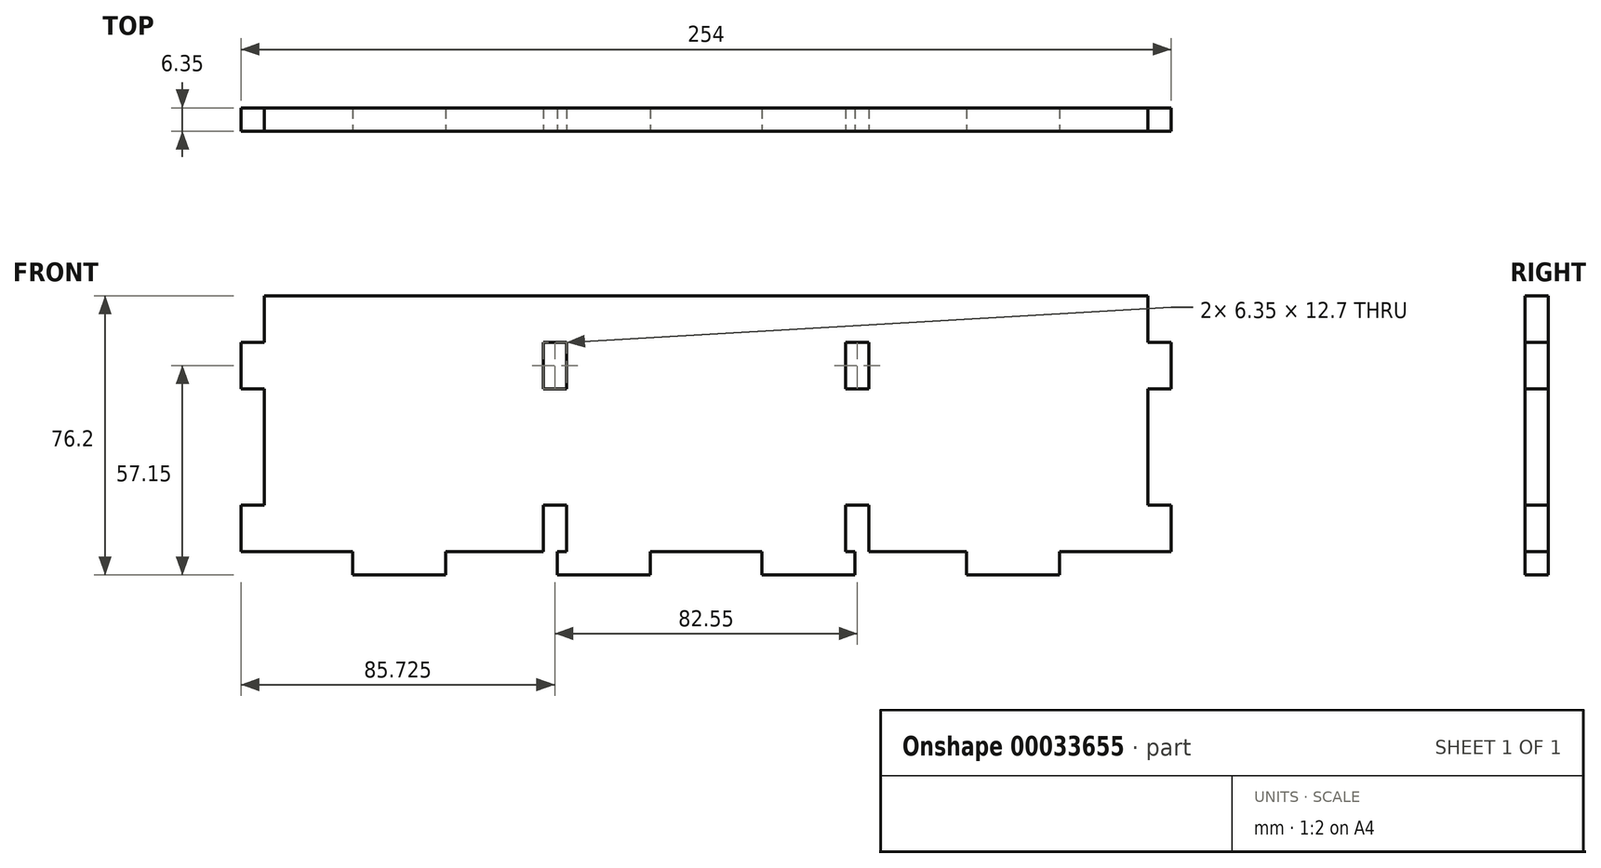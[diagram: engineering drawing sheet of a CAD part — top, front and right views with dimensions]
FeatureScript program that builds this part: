
annotation { "Feature Type Name" : "Feature", "Feature Type Description" : "" }
export const myFeature = defineFeature(function(context is Context, id is Id, definition is map)
    precondition{}
    {
        {
            var Q0;
            Q0=qCreatedBy(makeId("Front.planeOp"),FACE);
            var sketch = newSketch(context, id + "F0", { "sketchPlane" : qUnion([Q0])});
            skLineSegment(sketch, "E0.bottom", {"start": v(0, 0) * mm, "end": v(254, 0) * mm});
            skLineSegment(sketch, "E0.top", {"start": v(0, 76.2) * mm, "end": v(254, 76.2) * mm});
            skLineSegment(sketch, "E0.left", {"start": v(0, 0) * mm, "end": v(0, 76.2) * mm});
            skLineSegment(sketch, "E0.right", {"start": v(254, 0) * mm, "end": v(254, 76.2) * mm});
            skSolve(sketch);
        }
        {
            var Q0;
            Q0=makeQuery(id+"F0.imprint","IMPRINT",FACE,{"disambiguationData":[TD([[makeQuery(id+"F0.imprint","IMPRINT",EDGE,{"derivedFrom":sQuery(id+"F0.wireOp",EDGE,"E0.bottom")}),1.0]])]});
            extrude(context, id + "F1", {"entities" : qUnion([Q0]), "depth" : 6.35 * mm});
        }
        {
            var Q0;
            Q0=makeQuery(id+"F1.opExtrude","CAP_FACE",FACE,{"disambiguationData":[OSD([sQuery(id+"F0.wireOp",EDGE,"E0.bottom"),sQuery(id+"F0.wireOp",EDGE,"E0.top"),sQuery(id+"F0.wireOp",EDGE,"E0.left"),sQuery(id+"F0.wireOp",EDGE,"E0.right")])],"isStart":false});
            var sketch = newSketch(context, id + "F2", { "sketchPlane" : qUnion([Q0])});
            skLineSegment(sketch, "E1", {"start": v(127, 76.2) * mm, "end": v(127, 0) * mm, "construction": true});
            skLineSegment(sketch, "E2.bottom", {"start": v(0, 0) * mm, "end": v(6.35, 0) * mm});
            skLineSegment(sketch, "E2.top", {"start": v(0, 6.35) * mm, "end": v(6.35, 6.35) * mm});
            skLineSegment(sketch, "E2.left", {"start": v(0, 0) * mm, "end": v(0, 6.35) * mm});
            skLineSegment(sketch, "E2.right", {"start": v(6.35, 0) * mm, "end": v(6.35, 6.35) * mm});
            skLineSegment(sketch, "E3.bottom", {"start": v(0, 76.2) * mm, "end": v(6.35, 76.2) * mm});
            skLineSegment(sketch, "E3.top", {"start": v(0, 63.5) * mm, "end": v(6.35, 63.5) * mm});
            skLineSegment(sketch, "E3.left", {"start": v(0, 76.2) * mm, "end": v(0, 63.5) * mm});
            skLineSegment(sketch, "E3.right", {"start": v(6.35, 76.2) * mm, "end": v(6.35, 63.5) * mm});
            skLineSegment(sketch, "E4.bottom", {"start": v(0, 19.05) * mm, "end": v(6.35, 19.05) * mm});
            skLineSegment(sketch, "E4.top", {"start": v(0, 50.8) * mm, "end": v(6.35, 50.8) * mm});
            skLineSegment(sketch, "E4.left", {"start": v(0, 19.05) * mm, "end": v(0, 50.8) * mm});
            skLineSegment(sketch, "E4.right", {"start": v(6.35, 19.05) * mm, "end": v(6.35, 50.8) * mm});
            skLineSegment(sketch, "E5.MirrorCS", {"start": v(254, 6.35) * mm, "end": v(247.65, 6.35) * mm});
            skLineSegment(sketch, "E6.MirrorCS", {"start": v(254, 19.05) * mm, "end": v(247.65, 19.05) * mm});
            skLineSegment(sketch, "E7.MirrorCS", {"start": v(254, 50.8) * mm, "end": v(247.65, 50.8) * mm});
            skLineSegment(sketch, "E8.MirrorCS", {"start": v(254, 0) * mm, "end": v(247.65, 0) * mm});
            skLineSegment(sketch, "E9.MirrorCS", {"start": v(247.65, 76.2) * mm, "end": v(247.65, 63.5) * mm});
            skLineSegment(sketch, "E10.MirrorCS", {"start": v(247.65, 0) * mm, "end": v(247.65, 6.35) * mm});
            skLineSegment(sketch, "E11.MirrorCS", {"start": v(254, 0) * mm, "end": v(254, 6.35) * mm});
            skLineSegment(sketch, "E12.MirrorCS", {"start": v(254, 63.5) * mm, "end": v(247.65, 63.5) * mm});
            skLineSegment(sketch, "E13.MirrorCS", {"start": v(254, 76.2) * mm, "end": v(247.65, 76.2) * mm});
            skLineSegment(sketch, "E14.MirrorCS", {"start": v(254, 76.2) * mm, "end": v(254, 63.5) * mm});
            skLineSegment(sketch, "E15.MirrorCS", {"start": v(247.65, 19.05) * mm, "end": v(247.65, 50.8) * mm});
            skLineSegment(sketch, "E16.MirrorCS", {"start": v(254, 19.05) * mm, "end": v(254, 50.8) * mm});
            skSolve(sketch);
        }
        {
            var Q0;
            Q0=qSketchRegion(id+"F2",true);
            extrude(context, id + "F3", {"entities" : qUnion([Q0]), "operationType" : NewBodyOperationType.REMOVE, "endBound" : BoundingType.UP_TO_NEXT, "oppositeDirection" : true, "depth" : 25.4 * mm});
        }
        {
            var Q0;
            Q0=makeQuery(id+"F1.opExtrude","CAP_FACE",FACE,{"disambiguationData":[OSD([sQuery(id+"F0.wireOp",EDGE,"E0.bottom"),sQuery(id+"F0.wireOp",EDGE,"E0.top"),sQuery(id+"F0.wireOp",EDGE,"E0.left"),sQuery(id+"F0.wireOp",EDGE,"E0.right")])],"isStart":false});
            var sketch = newSketch(context, id + "F4", { "sketchPlane" : qUnion([Q0])});
            skLineSegment(sketch, "E17.bottom", {"start": v(0, 0) * mm, "end": v(30.48, 0) * mm});
            skLineSegment(sketch, "E17.top", {"start": v(0, 6.35) * mm, "end": v(30.48, 6.35) * mm});
            skLineSegment(sketch, "E17.left", {"start": v(0, 0) * mm, "end": v(0, 6.35) * mm});
            skLineSegment(sketch, "E17.right", {"start": v(30.48, 0) * mm, "end": v(30.48, 6.35) * mm});
            skLineSegment(sketch, "E18.1.0.0", {"start": v(86.36, 0) * mm, "end": v(86.36, 6.35) * mm});
            skLineSegment(sketch, "E18.1.0.1", {"start": v(55.88, 0) * mm, "end": v(55.88, 6.35) * mm});
            skLineSegment(sketch, "E18.1.0.2", {"start": v(55.88, 6.35) * mm, "end": v(86.36, 6.35) * mm});
            skLineSegment(sketch, "E18.1.0.3", {"start": v(55.88, 0) * mm, "end": v(86.36, 0) * mm});
            skLineSegment(sketch, "E18.2.0.0", {"start": v(142.24, 0) * mm, "end": v(142.24, 6.35) * mm});
            skLineSegment(sketch, "E18.2.0.1", {"start": v(111.76, 0) * mm, "end": v(111.76, 6.35) * mm});
            skLineSegment(sketch, "E18.2.0.2", {"start": v(111.76, 6.35) * mm, "end": v(142.24, 6.35) * mm});
            skLineSegment(sketch, "E18.2.0.3", {"start": v(111.76, 0) * mm, "end": v(142.24, 0) * mm});
            skLineSegment(sketch, "E18.3.0.0", {"start": v(198.12, 0) * mm, "end": v(198.12, 6.35) * mm});
            skLineSegment(sketch, "E18.3.0.1", {"start": v(167.64, 0) * mm, "end": v(167.64, 6.35) * mm});
            skLineSegment(sketch, "E18.3.0.2", {"start": v(167.64, 6.35) * mm, "end": v(198.12, 6.35) * mm});
            skLineSegment(sketch, "E18.3.0.3", {"start": v(167.64, 0) * mm, "end": v(198.12, 0) * mm});
            skLineSegment(sketch, "E18.4.0.0", {"start": v(254, 0) * mm, "end": v(254, 6.35) * mm});
            skLineSegment(sketch, "E18.4.0.1", {"start": v(223.52, 0) * mm, "end": v(223.52, 6.35) * mm});
            skLineSegment(sketch, "E18.4.0.2", {"start": v(223.52, 6.35) * mm, "end": v(254, 6.35) * mm});
            skLineSegment(sketch, "E18.4.0.3", {"start": v(223.52, 0) * mm, "end": v(254, 0) * mm});
            skLineSegment(sketch, "E18.direction1", {"start": v(30.48, 0) * mm, "end": v(86.36, 0) * mm, "construction": true});
            skSolve(sketch);
        }
        {
            var Q0;
            Q0=qSketchRegion(id+"F4",true);
            extrude(context, id + "F5", {"entities" : qUnion([Q0]), "operationType" : NewBodyOperationType.REMOVE, "endBound" : BoundingType.THROUGH_ALL, "oppositeDirection" : true, "depth" : 25.4 * mm});
        }
        {
            var Q0;
            Q0=makeQuery(id+"F1.opExtrude","CAP_FACE",FACE,{"disambiguationData":[OSD([sQuery(id+"F0.wireOp",EDGE,"E0.bottom"),sQuery(id+"F0.wireOp",EDGE,"E0.top"),sQuery(id+"F0.wireOp",EDGE,"E0.left"),sQuery(id+"F0.wireOp",EDGE,"E0.right")])],"isStart":false});
            var sketch = newSketch(context, id + "F6", { "sketchPlane" : qUnion([Q0])});
            skLineSegment(sketch, "E19.bottom", {"start": v(82.55, 6.35) * mm, "end": v(88.9, 6.35) * mm});
            skLineSegment(sketch, "E19.top", {"start": v(82.55, 19.05) * mm, "end": v(88.9, 19.05) * mm});
            skLineSegment(sketch, "E19.left", {"start": v(82.55, 6.35) * mm, "end": v(82.55, 19.05) * mm});
            skLineSegment(sketch, "E19.right", {"start": v(88.9, 6.35) * mm, "end": v(88.9, 19.05) * mm});
            skLineSegment(sketch, "E20", {"start": v(127, 76.2) * mm, "end": v(127, 0) * mm, "construction": true});
            skLineSegment(sketch, "E21.bottom", {"start": v(82.55, 50.8) * mm, "end": v(88.9, 50.8) * mm});
            skLineSegment(sketch, "E21.top", {"start": v(82.55, 63.5) * mm, "end": v(88.9, 63.5) * mm});
            skLineSegment(sketch, "E21.left", {"start": v(82.55, 50.8) * mm, "end": v(82.55, 63.5) * mm});
            skLineSegment(sketch, "E21.right", {"start": v(88.9, 50.8) * mm, "end": v(88.9, 63.5) * mm});
            skLineSegment(sketch, "E22.MirrorCS", {"start": v(165.1, 50.8) * mm, "end": v(165.1, 63.5) * mm});
            skLineSegment(sketch, "E23.MirrorCS", {"start": v(171.45, 50.8) * mm, "end": v(171.45, 63.5) * mm});
            skLineSegment(sketch, "E24.MirrorCS", {"start": v(171.45, 6.35) * mm, "end": v(165.1, 6.35) * mm});
            skLineSegment(sketch, "E25.MirrorCS", {"start": v(171.45, 19.05) * mm, "end": v(165.1, 19.05) * mm});
            skLineSegment(sketch, "E26.MirrorCS", {"start": v(171.45, 6.35) * mm, "end": v(171.45, 19.05) * mm});
            skLineSegment(sketch, "E27.MirrorCS", {"start": v(165.1, 6.35) * mm, "end": v(165.1, 19.05) * mm});
            skLineSegment(sketch, "E28.MirrorCS", {"start": v(171.45, 50.8) * mm, "end": v(165.1, 50.8) * mm});
            skLineSegment(sketch, "E29.MirrorCS", {"start": v(171.45, 63.5) * mm, "end": v(165.1, 63.5) * mm});
            skLineSegment(sketch, "E30.1.0.2", {"start": v(165.1, 63.5) * mm, "end": v(171.45, 63.5) * mm});
            skLineSegment(sketch, "E30.1.0.3", {"start": v(165.1, 50.8) * mm, "end": v(171.45, 50.8) * mm});
            skLineSegment(sketch, "E30.1.0.6", {"start": v(165.1, 19.05) * mm, "end": v(171.45, 19.05) * mm});
            skLineSegment(sketch, "E30.1.0.7", {"start": v(165.1, 6.35) * mm, "end": v(171.45, 6.35) * mm});
            skLineSegment(sketch, "E30.direction1", {"start": v(88.9, 50.8) * mm, "end": v(171.45, 50.8) * mm, "construction": true});
            skSolve(sketch);
        }
        {
            var Q0;
            Q0=qSketchRegion(id+"F6",true);
            extrude(context, id + "F7", {"entities" : qUnion([Q0]), "operationType" : NewBodyOperationType.REMOVE, "endBound" : BoundingType.THROUGH_ALL, "oppositeDirection" : true, "depth" : 25.4 * mm});
        }
    });
